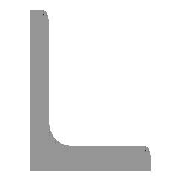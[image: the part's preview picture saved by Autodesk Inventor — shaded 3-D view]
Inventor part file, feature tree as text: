
AUTODESK INVENTOR PART (.ipt)
format: ipt  version: 2013 (Build 170138000, 138)  size: 129,536 bytes
history: native  units: mm (DEFAULTED — no unit token found)
features: other x4, plane x3, split x2, sketch x2
ambient origin geometry x8: Origin, YZ Plane, XZ Plane, XY Plane, X Axis, Y Axis, Z Axis, Center Point
bodies: Solid1 (feature_tree), Body (feature_tree)
feature tree (11):
  parser-record x1  (decoder bookkeeping rows leaked as tree rows — omitted from the tree; the rows remain in map.json)
  other  "Driven Length"
  other  "Start plane"
  other  "End plane"
  plane  "Work Plane4"
  split  "Split1"
  plane  "Work Plane5"
  split  "Split2"
  sketch  "Sketch3"  dims[d0=38.1mm]
  plane  "Work Plane3"
  sketch  "Sketch4"  dims[d1=38.1mm d2=4.7625mm d3=4.7625mm d4=561.975mm d5=0.0mm d10=0.0mm d11=0.0mm d12=-0.0mm d13=561.975mm d14=4.826mm d15=2.286mm d16=90.0deg d17=561.975mm]
